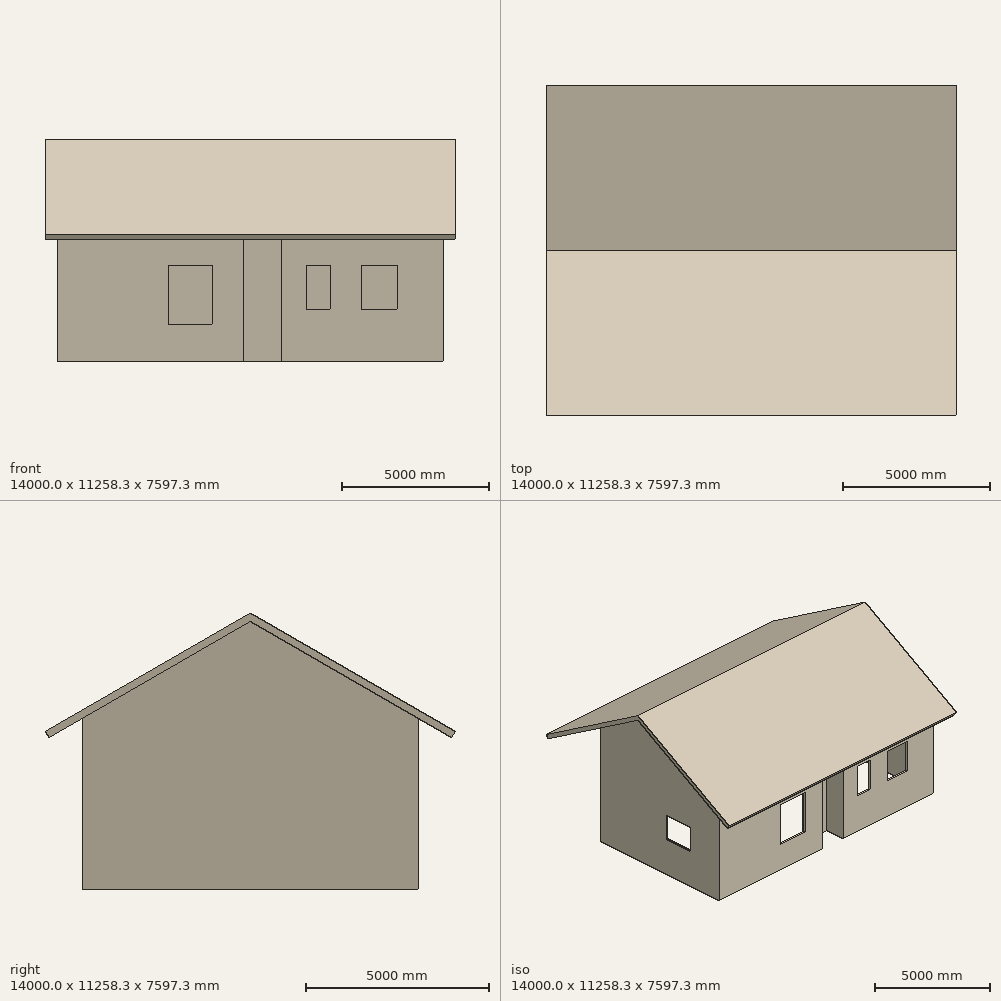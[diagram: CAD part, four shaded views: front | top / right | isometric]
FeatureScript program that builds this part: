
annotation { "Feature Type Name" : "Feature", "Feature Type Description" : "" }
export const myFeature = defineFeature(function(context is Context, id is Id, definition is map)
    precondition{}
    {
        {
            var Q0;
            Q0=qCreatedBy(makeId("Top.planeOp"),FACE);
            var sketch = newSketch(context, id + "F0", { "sketchPlane" : qUnion([Q0])});
            skLineSegment(sketch, "E0.bottom", {"start": v(100, 4500) * mm, "end": v(6500, 4500) * mm});
            skLineSegment(sketch, "E0.top", {"start": v(-6500, -4500) * mm, "end": v(-353.43, -4500) * mm});
            skLineSegment(sketch, "E0.left", {"start": v(-6500, 2609.87) * mm, "end": v(-6500, -4500) * mm});
            skLineSegment(sketch, "E0.right", {"start": v(6500, 4500) * mm, "end": v(6500, -4500) * mm});
            skPoint(sketch, "E0.middle", {"position": v(0, 0) * mm});
            skLineSegment(sketch, "E1", {"start": v(-353.43, -4500) * mm, "end": v(-353.43, -3500) * mm});
            skLineSegment(sketch, "E2", {"start": v(-353.43, -3500) * mm, "end": v(1146.57, -3500) * mm});
            skLineSegment(sketch, "E3", {"start": v(1146.57, -3500) * mm, "end": v(1146.57, -4500) * mm});
            skLineSegment(sketch, "E4.trimOffspring", {"start": v(1146.57, -4500) * mm, "end": v(6500, -4500) * mm});
            skLineSegment(sketch, "E5.0", {"start": v(-253.43, -3600) * mm, "end": v(1046.57, -3600) * mm});
            skLineSegment(sketch, "E5.1", {"start": v(-253.43, -4600) * mm, "end": v(-253.43, -3600) * mm});
            skLineSegment(sketch, "E5.2", {"start": v(1046.57, -3600) * mm, "end": v(1046.57, -4600) * mm});
            skLineSegment(sketch, "E5.3", {"start": v(-6600, -4600) * mm, "end": v(-253.43, -4600) * mm});
            skLineSegment(sketch, "E5.4", {"start": v(1046.57, -4600) * mm, "end": v(6600, -4600) * mm});
            skLineSegment(sketch, "E5.5", {"start": v(6600, 4600) * mm, "end": v(6600, -4600) * mm});
            skLineSegment(sketch, "E5.6", {"start": v(0, 4600) * mm, "end": v(6600, 4600) * mm});
            skLineSegment(sketch, "E5.7", {"start": v(-6600, 2609.87) * mm, "end": v(-6600, -4600) * mm});
            skLineSegment(sketch, "E6", {"start": v(0, 2709.87) * mm, "end": v(0, 4600) * mm});
            skLineSegment(sketch, "E7.0", {"start": v(100, 2609.87) * mm, "end": v(100, 4500) * mm});
            skLineSegment(sketch, "E8", {"start": v(100, 2609.87) * mm, "end": v(-6500, 2609.87) * mm});
            skLineSegment(sketch, "E9", {"start": v(0, 2709.87) * mm, "end": v(-6600, 2709.87) * mm});
            skLineSegment(sketch, "E10", {"start": v(-6600, 2709.87) * mm, "end": v(-6600, 2609.87) * mm});
            skSolve(sketch);
        }
        {
            var Q0;
            Q0=qCreatedBy(makeId("Right.planeOp"),FACE);
            var sketch = newSketch(context, id + "F1", { "sketchPlane" : qUnion([Q0])});
            skLineSegment(sketch, "E11", {"start": v(0, 7366.37) * mm, "end": v(-5529.17, 4174.1) * mm});
            skLineSegment(sketch, "E12", {"start": v(0, 7366.37) * mm, "end": v(5529.17, 4174.1) * mm});
            skLineSegment(sketch, "E13", {"start": v(-8602, 0) * mm, "end": v(-8602, 2400) * mm});
            skLineSegment(sketch, "E14.0", {"start": v(0, 7597.3) * mm, "end": v(5629.17, 4347.3) * mm});
            skLineSegment(sketch, "E14.1", {"start": v(0, 7597.3) * mm, "end": v(-5629.17, 4347.3) * mm});
            skLineSegment(sketch, "E15", {"start": v(-5629.17, 4347.3) * mm, "end": v(-5529.17, 4174.1) * mm});
            skLineSegment(sketch, "E16", {"start": v(5629.17, 4347.3) * mm, "end": v(5529.17, 4174.1) * mm});
            skSolve(sketch);
        }
        {
            var Q0;
            Q0=makeQuery(id+"F1.imprint","IMPRINT",FACE,{"disambiguationData":[TD([[makeQuery(id+"F1.imprint","IMPRINT",EDGE,{"derivedFrom":sQuery(id+"F1.wireOp",EDGE,"E11")}),-1.0]])]});
            var Q1;
            Q1=sQuery(id+"F1.wireOp",EDGE,"E12");
            var Q2;
            Q2=sQuery(id+"F1.wireOp",EDGE,"E11");
            extrude(context, id + "F2", {"entities" : qUnion([Q0]), "surfaceEntities" : qUnion([Q1, Q2]), "endBound" : BoundingType.SYMMETRIC, "depth" : 14000 * mm});
        }
        {
            var Q0;
            Q0=qSketchRegion(id+"F0",true);
            var Q1;
            Q1=makeQuery(id+"F2.opExtrude","SWEPT_FACE",FACE,{"disambiguationData":[OSD([sQuery(id+"F1.wireOp",EDGE,"E11")])]});
            var Q2;
            Q2=makeQuery(id+"F2.opExtrude","SWEPT_BODY",BODY,{"disambiguationData":[OSD([sQuery(id+"F1.wireOp",EDGE,"E11")])]});
            extrude(context, id + "F3", {"entities" : qUnion([Q0]), "endBound" : BoundingType.UP_TO_BODY, "endBoundEntityFace" : qUnion([Q1]), "endBoundEntityBody" : qUnion([Q2]), "depth" : 25 * mm});
        }
        {
            var Q0;
            Q0=makeQuery(id+"F3.opExtrude","SWEPT_FACE",FACE,{"disambiguationData":[OSD([sQuery(id+"F0.wireOp",EDGE,"E5.3")])]});
            var sketch = newSketch(context, id + "F4", { "sketchPlane" : qUnion([Q0])});
            skLineSegment(sketch, "E17.bottom", {"start": v(-2801.16, 3281.5) * mm, "end": v(-1301.16, 3281.5) * mm});
            skLineSegment(sketch, "E17.top", {"start": v(-2801.16, 1281.5) * mm, "end": v(-1301.16, 1281.5) * mm});
            skLineSegment(sketch, "E17.left", {"start": v(-2801.16, 3281.5) * mm, "end": v(-2801.16, 1281.5) * mm});
            skLineSegment(sketch, "E17.right", {"start": v(-1301.16, 3281.5) * mm, "end": v(-1301.16, 1281.5) * mm});
            skLineSegment(sketch, "E18.bottom", {"start": v(1926.85, 3281.5) * mm, "end": v(2726.85, 3281.5) * mm});
            skLineSegment(sketch, "E18.top", {"start": v(1926.85, 1781.5) * mm, "end": v(2726.85, 1781.5) * mm});
            skLineSegment(sketch, "E18.left", {"start": v(1926.85, 3281.5) * mm, "end": v(1926.85, 1781.5) * mm});
            skLineSegment(sketch, "E18.right", {"start": v(2726.85, 3281.5) * mm, "end": v(2726.85, 1781.5) * mm});
            skLineSegment(sketch, "E19.bottom", {"start": v(3807.08, 3281.5) * mm, "end": v(5007.08, 3281.5) * mm});
            skLineSegment(sketch, "E19.top", {"start": v(3807.08, 1781.5) * mm, "end": v(5007.08, 1781.5) * mm});
            skLineSegment(sketch, "E19.left", {"start": v(3807.08, 3281.5) * mm, "end": v(3807.08, 1781.5) * mm});
            skLineSegment(sketch, "E19.right", {"start": v(5007.08, 3281.5) * mm, "end": v(5007.08, 1781.5) * mm});
            skSolve(sketch);
        }
        {
            var Q0;
            Q0=qSketchRegion(id+"F4",true);
            var Q1;
            Q1=makeQuery(id+"F3.opExtrude","SWEPT_FACE",FACE,{"disambiguationData":[OSD([sQuery(id+"F0.wireOp",EDGE,"E0.top")])]});
            extrude(context, id + "F5", {"entities" : qUnion([Q0, Q1]), "operationType" : NewBodyOperationType.REMOVE, "endBound" : BoundingType.UP_TO_NEXT, "oppositeDirection" : true, "depth" : 25 * mm});
        }
        {
            var Q0;
            Q0=makeQuery(id+"F3.opExtrude","SWEPT_FACE",FACE,{"disambiguationData":[OSD([sQuery(id+"F0.wireOp",EDGE,"E5.7"),sQuery(id+"F0.wireOp",EDGE,"E10")])]});
            var sketch = newSketch(context, id + "F6", { "sketchPlane" : qUnion([Q0])});
            skLineSegment(sketch, "E20.bottom", {"start": v(1354.84, 2967.69) * mm, "end": v(2854.84, 2967.69) * mm});
            skLineSegment(sketch, "E20.top", {"start": v(1354.84, 1767.69) * mm, "end": v(2854.84, 1767.69) * mm});
            skLineSegment(sketch, "E20.left", {"start": v(1354.84, 2967.69) * mm, "end": v(1354.84, 1767.69) * mm});
            skLineSegment(sketch, "E20.right", {"start": v(2854.84, 2967.69) * mm, "end": v(2854.84, 1767.69) * mm});
            skSolve(sketch);
        }
        {
            var Q0;
            Q0=qSketchRegion(id+"F6",true);
            var Q1;
            Q1=makeQuery(id+"F3.opExtrude","SWEPT_FACE",FACE,{"disambiguationData":[OSD([sQuery(id+"F0.wireOp",EDGE,"E0.left")])]});
            extrude(context, id + "F7", {"entities" : qUnion([Q0]), "operationType" : NewBodyOperationType.REMOVE, "endBound" : BoundingType.UP_TO_SURFACE, "oppositeDirection" : true, "endBoundEntityFace" : qUnion([Q1]), "depth" : 25 * mm});
        }
    });
